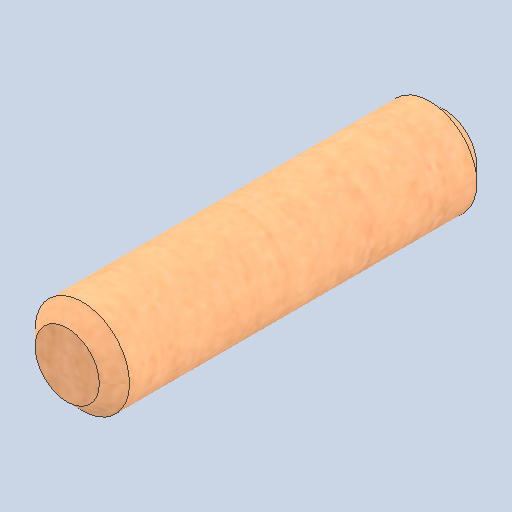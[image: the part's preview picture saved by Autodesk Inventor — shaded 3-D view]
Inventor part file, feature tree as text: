
AUTODESK INVENTOR PART (.ipt)
format: ipt  version: 2024 (Build 280153000, 153)  size: 307,712 bytes
history: native  units: in
note: dims shown in document units (in); Inventor stores cm internally (conversion verified against a paired STEP export)
features: extrude x1, chamfer x1, direct_edit x1, sketch x1, other x1
ambient origin geometry x8: Origin, YZ Plane, XZ Plane, XY Plane, X Axis, Y Axis, Z Axis, Center Point
bodies: Solid1 (feature_tree)
feature tree (5):
  extrude  "Extrusion1"  Depth=0.3937in TaperAngle=0.0deg
  chamfer  "Chamfer1"  Distance=0.015in Angle=45.0deg
  direct_edit  "Direct Edit1"
  sketch  "Sketch1"  dims[d0=0.0938in d1=0.375in d2=0.0in d3=0.015in d4=0.125in d5=45.0deg d6=3.937in d7=0.3937in d8=0.3937in]
  other  "Scale1"
